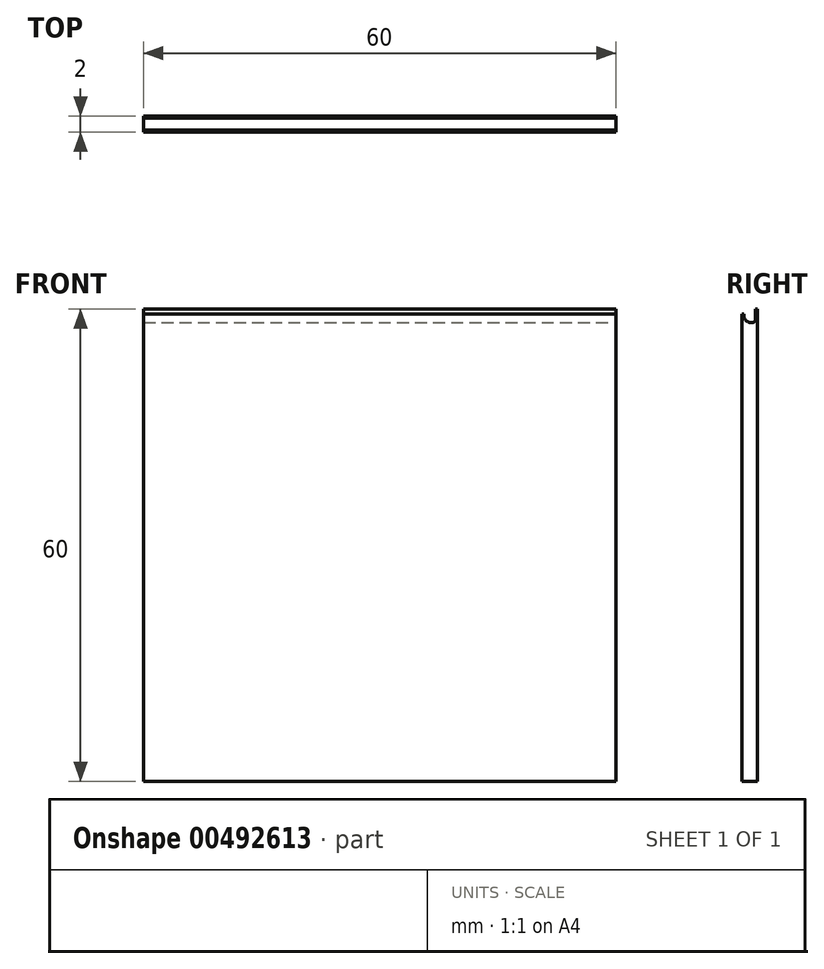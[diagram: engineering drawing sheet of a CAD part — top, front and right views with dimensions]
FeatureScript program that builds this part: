
annotation { "Feature Type Name" : "Feature", "Feature Type Description" : "" }
export const myFeature = defineFeature(function(context is Context, id is Id, definition is map)
    precondition{}
    {
        {
            var Q0;
            Q0=qCreatedBy(makeId("Front.planeOp"),FACE);
            var sketch = newSketch(context, id + "F0", { "sketchPlane" : qUnion([Q0])});
            skLineSegment(sketch, "E0.bottom", {"start": v(-43.07, 48.69) * mm, "end": v(16.93, 48.69) * mm});
            skLineSegment(sketch, "E0.top", {"start": v(-43.07, -11.31) * mm, "end": v(16.93, -11.31) * mm});
            skLineSegment(sketch, "E0.left", {"start": v(-43.07, 48.69) * mm, "end": v(-43.07, -11.31) * mm});
            skLineSegment(sketch, "E0.right", {"start": v(16.93, 48.69) * mm, "end": v(16.93, -11.31) * mm});
            skSolve(sketch);
        }
        {
            var Q0;
            Q0=makeQuery(id+"F0.imprint","IMPRINT",FACE,{"disambiguationData":[TD([[makeQuery(id+"F0.imprint","IMPRINT",EDGE,{"derivedFrom":sQuery(id+"F0.wireOp",EDGE,"E0.bottom")}),-1.0]])]});
            extrude(context, id + "F1", {"entities" : qUnion([Q0]), "depth" : 2 * mm});
        }
        {
            var Q0;
            Q0=makeQuery(id+"F1.opExtrude","SWEPT_FACE",FACE,{"disambiguationData":[OSD([sQuery(id+"F0.wireOp",EDGE,"E0.right")])]});
            var sketch = newSketch(context, id + "F2", { "sketchPlane" : qUnion([Q0])});
            skPoint(sketch, "E1.visualSharp", {"position": v(-0.93, 47.28) * mm});
            skLineSegment(sketch, "E2", {"start": v(0, 48.69) * mm, "end": v(-0.25, 48.69) * mm});
            skLineSegment(sketch, "E3", {"start": v(-0.25, 48.69) * mm, "end": v(-0.25, 47.45) * mm});
            skLineSegment(sketch, "E4", {"start": v(-0.75, 46.95) * mm, "end": v(-0.76, 46.95) * mm});
            skLineSegment(sketch, "E5", {"start": v(-1.76, 47.95) * mm, "end": v(-1.76, 48.07) * mm});
            skLineSegment(sketch, "E6", {"start": v(-1.76, 48.07) * mm, "end": v(-2, 48.07) * mm});
            skLineSegment(sketch, "E7", {"start": v(-2, 48.07) * mm, "end": v(-2, 48.69) * mm});
            skLineSegment(sketch, "E8", {"start": v(-2, 48.69) * mm, "end": v(-0.25, 48.69) * mm});
            skPoint(sketch, "E9.visualSharp", {"position": v(-1.76, 46.95) * mm});
            skArc(sketch, "E9.filletArc", {"start": v(-1.76, 47.95) * mm, "mid": v(-1.46, 47.24) * mm, "end": v(-0.76, 46.95) * mm});
            skPoint(sketch, "E10.visualSharp", {"position": v(-0.25, 46.95) * mm});
            skArc(sketch, "E10.filletArc", {"start": v(-0.75, 46.95) * mm, "mid": v(-0.4, 47.1) * mm, "end": v(-0.25, 47.45) * mm});
            skSolve(sketch);
        }
        {
            var Q0;
            Q0 = qSketchRegion(id + "F2", true);
            extrude(context, id + "F3", {"entities" : qUnion([Q0]), "operationType" : NewBodyOperationType.REMOVE, "oppositeDirection" : true, "depth" : 60 * mm});
        }
    });
